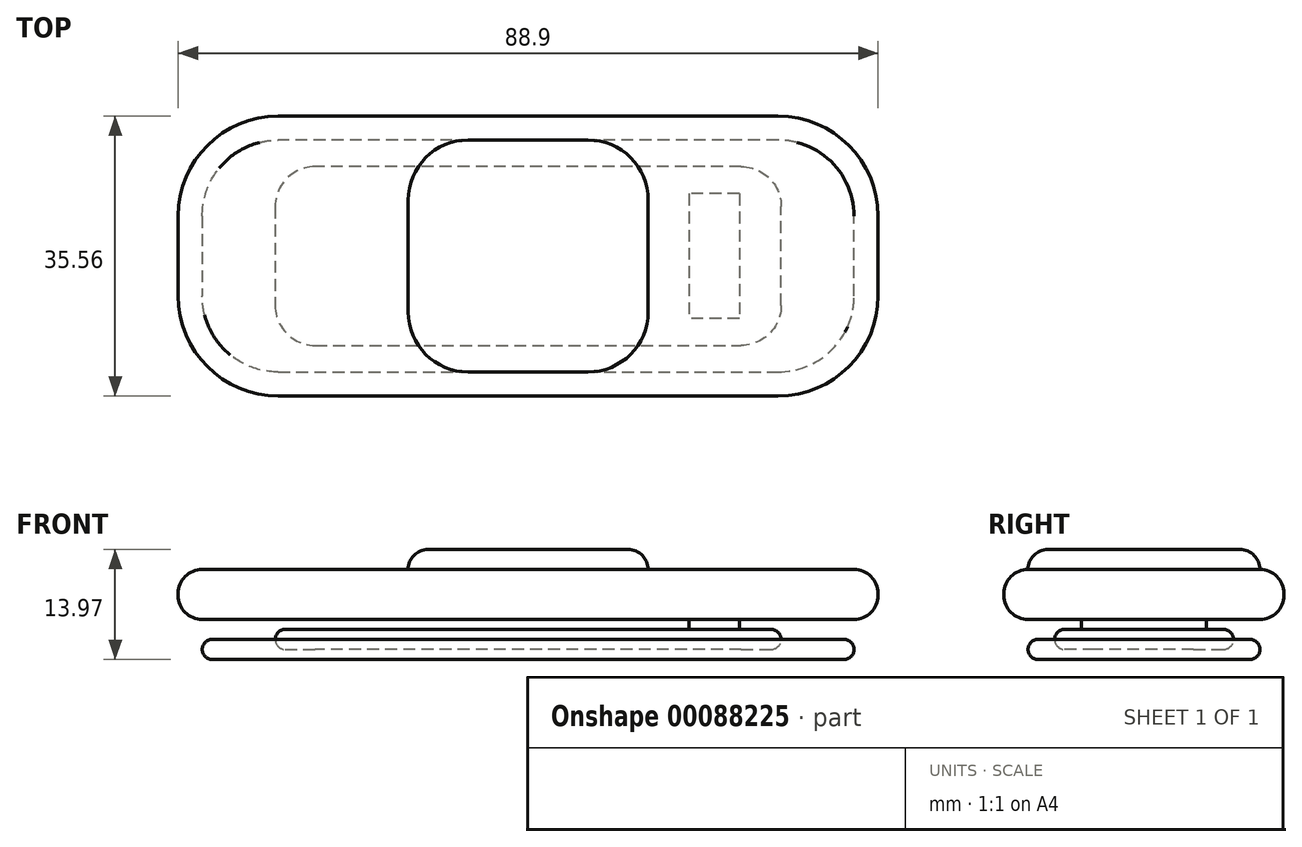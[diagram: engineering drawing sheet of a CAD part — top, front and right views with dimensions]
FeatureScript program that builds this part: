
annotation { "Feature Type Name" : "Feature", "Feature Type Description" : "" }
export const myFeature = defineFeature(function(context is Context, id is Id, definition is map)
    precondition{}
    {
        {
            var Q0;
            Q0=qCreatedBy(makeId("Top.planeOp"),FACE);
            var sketch = newSketch(context, id + "F0", { "sketchPlane" : qUnion([Q0])});
            skLineSegment(sketch, "E0.bottom", {"start": v(44.45, -17.78) * mm, "end": v(-44.45, -17.78) * mm});
            skLineSegment(sketch, "E0.top", {"start": v(44.45, 17.78) * mm, "end": v(-44.45, 17.78) * mm});
            skLineSegment(sketch, "E0.left", {"start": v(44.45, -17.78) * mm, "end": v(44.45, 17.78) * mm});
            skLineSegment(sketch, "E0.right", {"start": v(-44.45, -17.78) * mm, "end": v(-44.45, 17.78) * mm});
            skPoint(sketch, "E0.middle", {"position": v(0, 0) * mm});
            skSolve(sketch);
        }
        {
            var Q0;
            Q0=makeQuery(id+"F0.imprint","IMPRINT",FACE,{"disambiguationData":[TD([[makeQuery(id+"F0.imprint","IMPRINT",EDGE,{"derivedFrom":sQuery(id+"F0.wireOp",EDGE,"E0.bottom")}),-1.0]])]});
            extrude(context, id + "F1", {"entities" : qUnion([Q0]), "depth" : 6.35 * mm});
        }
        {
            var Q0;
            Q0=makeQuery(id+"F1.opExtrude","SWEPT_EDGE",EDGE,{"disambiguationData":[OSD([sQuery(id+"F0.wireOp",EDGE,"E0.top"),sQuery(id+"F0.wireOp",EDGE,"E0.right")])]});
            var Q1;
            Q1=makeQuery(id+"F1.opExtrude","SWEPT_EDGE",EDGE,{"disambiguationData":[OSD([sQuery(id+"F0.wireOp",EDGE,"E0.bottom"),sQuery(id+"F0.wireOp",EDGE,"E0.right")])]});
            var Q2;
            Q2=makeQuery(id+"F1.opExtrude","SWEPT_EDGE",EDGE,{"disambiguationData":[OSD([sQuery(id+"F0.wireOp",EDGE,"E0.top"),sQuery(id+"F0.wireOp",EDGE,"E0.left")])]});
            var Q3;
            Q3=makeQuery(id+"F1.opExtrude","SWEPT_EDGE",EDGE,{"disambiguationData":[OSD([sQuery(id+"F0.wireOp",EDGE,"E0.bottom"),sQuery(id+"F0.wireOp",EDGE,"E0.left")])]});
            fillet(context, id + "F2", {"entities" : qUnion([Q0, Q1, Q2, Q3]), "radius" : 12.7 * mm, "tangentPropagation" : true, "allowEdgeOverflow" : false});
        }
        {
            var Q0;
            Q0=makeQuery(id+"F1.opExtrude","CAP_FACE",FACE,{"disambiguationData":[OSD([sQuery(id+"F0.wireOp",EDGE,"E0.bottom"),sQuery(id+"F0.wireOp",EDGE,"E0.top"),sQuery(id+"F0.wireOp",EDGE,"E0.left"),sQuery(id+"F0.wireOp",EDGE,"E0.right")])],"isStart":false});
            var Q1;
            Q1=makeQuery(id+"F1.opExtrude","CAP_FACE",FACE,{"disambiguationData":[OSD([sQuery(id+"F0.wireOp",EDGE,"E0.bottom"),sQuery(id+"F0.wireOp",EDGE,"E0.top"),sQuery(id+"F0.wireOp",EDGE,"E0.left"),sQuery(id+"F0.wireOp",EDGE,"E0.right")])],"isStart":true});
            fillet(context, id + "F3", {"entities" : qUnion([Q0, Q1]), "radius" : 3.05 * mm, "tangentPropagation" : true, "allowEdgeOverflow" : false});
        }
        {
            var Q0;
            Q0=makeQuery(id+"F1.opExtrude","CAP_FACE",FACE,{"disambiguationData":[OSD([sQuery(id+"F0.wireOp",EDGE,"E0.bottom"),sQuery(id+"F0.wireOp",EDGE,"E0.top"),sQuery(id+"F0.wireOp",EDGE,"E0.left"),sQuery(id+"F0.wireOp",EDGE,"E0.right")])],"isStart":true});
            var sketch = newSketch(context, id + "F4", { "sketchPlane" : qUnion([Q0])});
            skLineSegment(sketch, "E1.0", {"start": v(31.75, 14.73) * mm, "end": v(-31.75, 14.73) * mm});
            skLineSegment(sketch, "E2.0", {"start": v(-31.75, -14.73) * mm, "end": v(31.75, -14.73) * mm});
            skArc(sketch, "E3.0", {"start": v(-31.75, 14.73) * mm, "mid": v(-38.57, 11.9) * mm, "end": v(-41.4, 5.08) * mm});
            skLineSegment(sketch, "E4.0", {"start": v(-41.4, 5.08) * mm, "end": v(-41.4, -5.08) * mm});
            skArc(sketch, "E5.0", {"start": v(-41.4, -5.08) * mm, "mid": v(-38.57, -11.9) * mm, "end": v(-31.75, -14.73) * mm});
            skArc(sketch, "E6.0", {"start": v(31.75, -14.73) * mm, "mid": v(38.57, -11.9) * mm, "end": v(41.4, -5.08) * mm});
            skArc(sketch, "E7.0", {"start": v(41.4, 5.08) * mm, "mid": v(38.57, 11.9) * mm, "end": v(31.75, 14.73) * mm});
            skLineSegment(sketch, "E8.0", {"start": v(41.4, -5.08) * mm, "end": v(41.4, 5.08) * mm});
            skSolve(sketch);
        }
        {
            var Q0;
            Q0=qCreatedBy(makeId("Top.planeOp"),FACE);
            cPlane(context, id + "F5", {"entities" : qUnion([Q0]), "cplaneType" : CPlaneType.OFFSET, "offset" : 5.08 * mm, "oppositeDirection" : true, "width" : 152.4 * mm, "height" : 152.4 * mm});
        }
        {
            var Q0;
            Q0=qCreatedBy(id+"F5.planeOp",FACE);
            var sketch = newSketch(context, id + "F6", { "sketchPlane" : qUnion([Q0])});
            skLineSegment(sketch, "E9.0.0", {"start": v(31.75, -14.73) * mm, "end": v(-31.75, -14.73) * mm});
            skArc(sketch, "E9.0.1", {"start": v(-31.75, -14.73) * mm, "mid": v(-38.57, -11.9) * mm, "end": v(-41.4, -5.08) * mm});
            skLineSegment(sketch, "E9.0.2", {"start": v(-41.4, -5.08) * mm, "end": v(-41.4, 5.08) * mm});
            skArc(sketch, "E9.0.3", {"start": v(-41.4, 5.08) * mm, "mid": v(-38.57, 11.9) * mm, "end": v(-31.75, 14.73) * mm});
            skLineSegment(sketch, "E9.0.4", {"start": v(-31.75, 14.73) * mm, "end": v(31.75, 14.73) * mm});
            skArc(sketch, "E9.0.5", {"start": v(31.75, 14.73) * mm, "mid": v(38.57, 11.9) * mm, "end": v(41.4, 5.08) * mm});
            skLineSegment(sketch, "E9.0.6", {"start": v(41.4, 5.08) * mm, "end": v(41.4, -5.08) * mm});
            skArc(sketch, "E9.0.7", {"start": v(41.4, -5.08) * mm, "mid": v(38.57, -11.9) * mm, "end": v(31.75, -14.73) * mm});
            skSolve(sketch);
        }
        {
            var Q0;
            Q0=makeQuery(id+"F6.imprint","IMPRINT",FACE,{"disambiguationData":[TD([[makeQuery(id+"F6.imprint","IMPRINT",EDGE,{"derivedFrom":sQuery(id+"F6.wireOp",EDGE,"E9.0.0")}),-1.0]])]});
            extrude(context, id + "F7", {"entities" : qUnion([Q0]), "depth" : 2.54 * mm});
        }
        {
            var Q0;
            Q0=makeQuery(id+"F7.opExtrude","CAP_EDGE",EDGE,{"disambiguationData":[OSD([sQuery(id+"F6.wireOp",EDGE,"E9.0.4")])],"isStart":true});
            var Q1;
            Q1=makeQuery(id+"F7.opExtrude","CAP_EDGE",EDGE,{"disambiguationData":[OSD([sQuery(id+"F6.wireOp",EDGE,"E9.0.3")])],"isStart":false});
            fillet(context, id + "F8", {"entities" : qUnion([Q0, Q1]), "radius" : 1.27 * mm, "tangentPropagation" : true, "allowEdgeOverflow" : false});
        }
        {
            var Q0;
            Q0=makeQuery(id+"F1.opExtrude","CAP_FACE",FACE,{"disambiguationData":[OSD([sQuery(id+"F0.wireOp",EDGE,"E0.bottom"),sQuery(id+"F0.wireOp",EDGE,"E0.top"),sQuery(id+"F0.wireOp",EDGE,"E0.left"),sQuery(id+"F0.wireOp",EDGE,"E0.right")])],"isStart":false});
            var sketch = newSketch(context, id + "F9", { "sketchPlane" : qUnion([Q0])});
            skLineSegment(sketch, "E10.bottom", {"start": v(15.24, -14.73) * mm, "end": v(-15.24, -14.73) * mm});
            skLineSegment(sketch, "E10.top", {"start": v(15.24, 14.73) * mm, "end": v(-15.24, 14.73) * mm});
            skLineSegment(sketch, "E10.left", {"start": v(15.24, -14.73) * mm, "end": v(15.24, 14.73) * mm});
            skLineSegment(sketch, "E10.right", {"start": v(-15.24, -14.73) * mm, "end": v(-15.24, 14.73) * mm});
            skPoint(sketch, "E10.middle", {"position": v(0, 0) * mm});
            skSolve(sketch);
        }
        {
            var Q0;
            Q0=makeQuery(id+"F9.imprint","IMPRINT",FACE,{"disambiguationData":[TD([[makeQuery(id+"F9.imprint","IMPRINT",EDGE,{"derivedFrom":sQuery(id+"F9.wireOp",EDGE,"E10.bottom")}),1.0]])]});
            extrude(context, id + "F10", {"entities" : qUnion([Q0]), "operationType" : NewBodyOperationType.ADD, "depth" : 2.54 * mm});
        }
        {
            var Q0;
            Q0=makeQuery(id+"F10.opExtrude","SWEPT_EDGE",EDGE,{"disambiguationData":[OSD([sQuery(id+"F0.wireOp",EDGE,"E0.bottom"),sQuery(id+"F0.wireOp",EDGE,"E0.top"),sQuery(id+"F0.wireOp",EDGE,"E0.left"),sQuery(id+"F0.wireOp",EDGE,"E0.right"),sQuery(id+"F9.wireOp",EDGE,"E10.bottom"),sQuery(id+"F9.wireOp",EDGE,"E10.right")])]});
            var Q1;
            Q1=makeQuery(id+"F10.opExtrude","SWEPT_EDGE",EDGE,{"disambiguationData":[OSD([sQuery(id+"F0.wireOp",EDGE,"E0.bottom"),sQuery(id+"F0.wireOp",EDGE,"E0.top"),sQuery(id+"F0.wireOp",EDGE,"E0.left"),sQuery(id+"F0.wireOp",EDGE,"E0.right"),sQuery(id+"F9.wireOp",EDGE,"E10.top"),sQuery(id+"F9.wireOp",EDGE,"E10.right")])]});
            var Q2;
            Q2=makeQuery(id+"F10.opExtrude","SWEPT_EDGE",EDGE,{"disambiguationData":[OSD([sQuery(id+"F0.wireOp",EDGE,"E0.bottom"),sQuery(id+"F0.wireOp",EDGE,"E0.top"),sQuery(id+"F0.wireOp",EDGE,"E0.left"),sQuery(id+"F0.wireOp",EDGE,"E0.right"),sQuery(id+"F9.wireOp",EDGE,"E10.bottom"),sQuery(id+"F9.wireOp",EDGE,"E10.left")])]});
            var Q3;
            Q3=makeQuery(id+"F10.opExtrude","SWEPT_EDGE",EDGE,{"disambiguationData":[OSD([sQuery(id+"F0.wireOp",EDGE,"E0.bottom"),sQuery(id+"F0.wireOp",EDGE,"E0.top"),sQuery(id+"F0.wireOp",EDGE,"E0.left"),sQuery(id+"F0.wireOp",EDGE,"E0.right"),sQuery(id+"F9.wireOp",EDGE,"E10.top"),sQuery(id+"F9.wireOp",EDGE,"E10.left")])]});
            fillet(context, id + "F11", {"entities" : qUnion([Q0, Q1, Q2, Q3]), "radius" : 7.62 * mm, "tangentPropagation" : true, "allowEdgeOverflow" : false});
        }
        {
            var Q0;
            Q0=makeQuery(id+"F10.opExtrude","CAP_FACE",FACE,{"disambiguationData":[OSD([sQuery(id+"F9.wireOp",EDGE,"E10.bottom"),sQuery(id+"F9.wireOp",EDGE,"E10.top"),sQuery(id+"F9.wireOp",EDGE,"E10.left"),sQuery(id+"F9.wireOp",EDGE,"E10.right")])],"isStart":false});
            fillet(context, id + "F12", {"entities" : qUnion([Q0]), "radius" : 2.54 * mm, "tangentPropagation" : true, "allowEdgeOverflow" : false});
        }
        {
            var Q0;
            Q0=makeQuery(id+"F4.imprint","IMPRINT",FACE,{"disambiguationData":[TD([[makeQuery(id+"F4.imprint","IMPRINT",EDGE,{"derivedFrom":sQuery(id+"F4.wireOp",EDGE,"E1.0")}),1.0]])]});
            var sketch = newSketch(context, id + "F13", { "sketchPlane" : qUnion([Q0])});
            skLineSegment(sketch, "E11.bottom", {"start": v(26.83, -7.93) * mm, "end": v(20.41, -7.93) * mm});
            skLineSegment(sketch, "E11.top", {"start": v(26.83, 7.93) * mm, "end": v(20.41, 7.93) * mm});
            skLineSegment(sketch, "E11.left", {"start": v(26.83, -7.93) * mm, "end": v(26.83, 7.93) * mm});
            skLineSegment(sketch, "E11.right", {"start": v(20.41, -7.93) * mm, "end": v(20.41, 7.93) * mm});
            skPoint(sketch, "E11.middle", {"position": v(23.62, 0) * mm});
            skLineSegment(sketch, "E12.0", {"start": v(41.4, -5.08) * mm, "end": v(41.4, 5.08) * mm, "construction": true});
            skLineSegment(sketch, "E13", {"start": v(23.62, 0) * mm, "end": v(41.4, 0) * mm, "construction": true});
            skSolve(sketch);
        }
        {
            var Q0;
            Q0=makeQuery(id+"F13.imprint","IMPRINT",FACE,{"disambiguationData":[TD([[makeQuery(id+"F13.imprint","IMPRINT",EDGE,{"derivedFrom":sQuery(id+"F13.wireOp",EDGE,"E11.bottom")}),-1.0]])]});
            extrude(context, id + "F14", {"entities" : qUnion([Q0]), "operationType" : NewBodyOperationType.ADD, "depth" : 1.27 * mm});
        }
        {
            var Q0;
            Q0=makeQuery(id+"F14.opExtrude","CAP_FACE",FACE,{"disambiguationData":[OSD([sQuery(id+"F13.wireOp",EDGE,"E11.bottom"),sQuery(id+"F13.wireOp",EDGE,"E11.top"),sQuery(id+"F13.wireOp",EDGE,"E11.left"),sQuery(id+"F13.wireOp",EDGE,"E11.right")])],"isStart":false});
            var sketch = newSketch(context, id + "F15", { "sketchPlane" : qUnion([Q0])});
            skPoint(sketch, "E14.0", {"position": v(0, 0) * mm});
            skLineSegment(sketch, "E15.bottom", {"start": v(32.13, -11.36) * mm, "end": v(-32.13, -11.36) * mm});
            skLineSegment(sketch, "E15.top", {"start": v(32.13, 11.36) * mm, "end": v(-32.13, 11.36) * mm});
            skLineSegment(sketch, "E15.left", {"start": v(32.13, -11.36) * mm, "end": v(32.13, 11.36) * mm});
            skLineSegment(sketch, "E15.right", {"start": v(-32.13, -11.36) * mm, "end": v(-32.13, 11.36) * mm});
            skSolve(sketch);
        }
        {
            var Q0;
            Q0=makeQuery(id+"F15.imprint","IMPRINT",FACE,{"disambiguationData":[TD([[makeQuery(id+"F15.imprint","IMPRINT",EDGE,{"derivedFrom":sQuery(id+"F15.wireOp",EDGE,"E15.bottom")}),-1.0]])]});
            var Q1;
            Q1=makeQuery(id+"F15.imprint","IMPRINT",FACE,{"disambiguationData":[TD([[makeQuery(id+"F15.imprint","IMPRINT",EDGE,{"derivedFrom":makeQuery(id+"F14.opExtrude","CAP_EDGE",EDGE,{"disambiguationData":[OSD([sQuery(id+"F13.wireOp",EDGE,"E11.bottom")])],"isStart":false})}),-1.0]])]});
            extrude(context, id + "F16", {"entities" : qUnion([Q0, Q1]), "depth" : 2.54 * mm});
        }
        {
            var Q0;
            Q0=makeQuery(id+"F16.opExtrude","SWEPT_EDGE",EDGE,{"disambiguationData":[OSD([sQuery(id+"F15.wireOp",EDGE,"E15.bottom"),sQuery(id+"F15.wireOp",EDGE,"E15.left")])]});
            var Q1;
            Q1=makeQuery(id+"F16.opExtrude","SWEPT_EDGE",EDGE,{"disambiguationData":[OSD([sQuery(id+"F15.wireOp",EDGE,"E15.top"),sQuery(id+"F15.wireOp",EDGE,"E15.left")])]});
            var Q2;
            Q2=makeQuery(id+"F16.opExtrude","SWEPT_EDGE",EDGE,{"disambiguationData":[OSD([sQuery(id+"F15.wireOp",EDGE,"E15.top"),sQuery(id+"F15.wireOp",EDGE,"E15.right")])]});
            var Q3;
            Q3=makeQuery(id+"F16.opExtrude","SWEPT_EDGE",EDGE,{"disambiguationData":[OSD([sQuery(id+"F15.wireOp",EDGE,"E15.bottom"),sQuery(id+"F15.wireOp",EDGE,"E15.right")])]});
            fillet(context, id + "F17", {"entities" : qUnion([Q0, Q1, Q2, Q3]), "radius" : 5.08 * mm, "tangentPropagation" : true, "allowEdgeOverflow" : false});
        }
        {
            var Q0;
            Q0=makeQuery(id+"F16.opExtrude","CAP_FACE",FACE,{"disambiguationData":[OSD([sQuery(id+"F15.wireOp",EDGE,"E15.bottom"),sQuery(id+"F15.wireOp",EDGE,"E15.top"),sQuery(id+"F15.wireOp",EDGE,"E15.left"),sQuery(id+"F15.wireOp",EDGE,"E15.right")])],"isStart":false});
            var Q1;
            Q1=makeQuery(id+"F16.opExtrude","CAP_EDGE",EDGE,{"disambiguationData":[OSD([sQuery(id+"F15.wireOp",EDGE,"E15.top")])],"isStart":true});
            fillet(context, id + "F18", {"entities" : qUnion([Q0, Q1]), "radius" : 1.27 * mm, "tangentPropagation" : true, "allowEdgeOverflow" : false});
        }
    });
